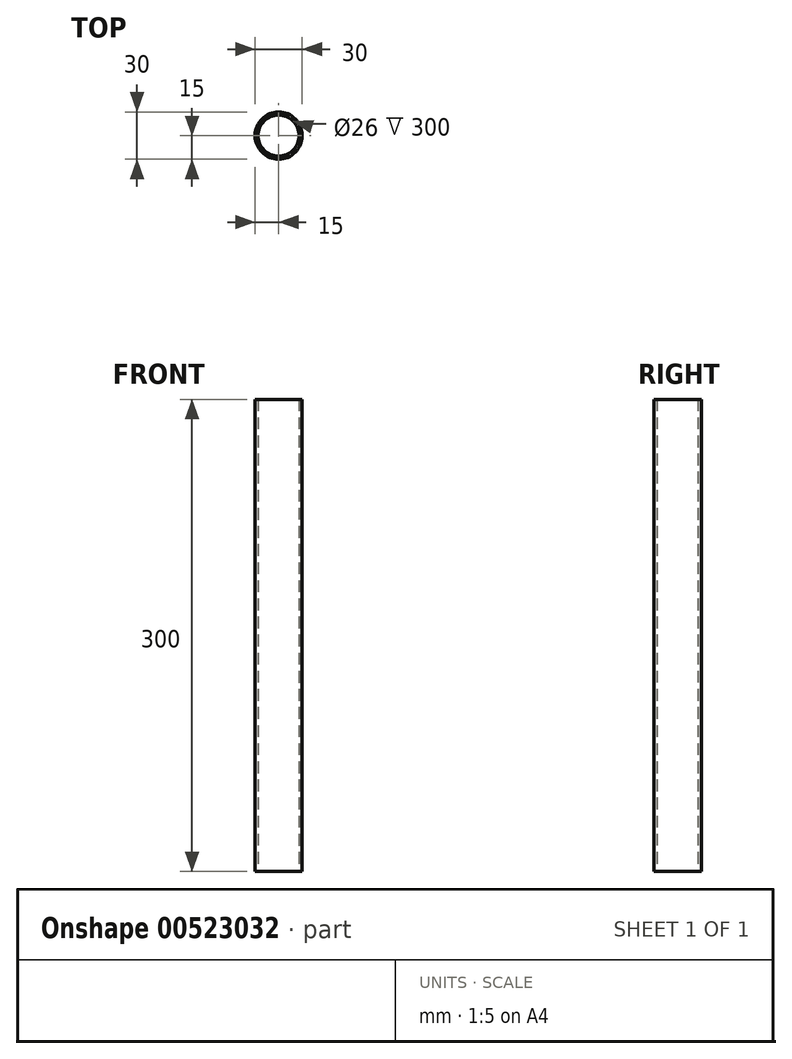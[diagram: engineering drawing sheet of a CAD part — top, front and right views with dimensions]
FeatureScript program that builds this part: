
annotation { "Feature Type Name" : "Feature", "Feature Type Description" : "" }
export const myFeature = defineFeature(function(context is Context, id is Id, definition is map)
    precondition{}
    {
        {
            var Q0;
            Q0=qCreatedBy(makeId("Top.planeOp"),FACE);
            var sketch = newSketch(context, id + "F0", { "sketchPlane" : qUnion([Q0])});
            skCircle(sketch, "E0", {"center": v(0, 0) * mm, "radius": 15 * mm});
            skCircle(sketch, "E1", {"center": v(0, 0) * mm, "radius": 13 * mm});
            skSolve(sketch);
        }
        {
            var Q0;
            Q0 = qSketchRegion(id + "F0", true);
            extrude(context, id + "F1", {"entities" : qUnion([Q0]), "depth" : 300 * mm, "offsetDistance" : 25 * mm});
        }
    });
